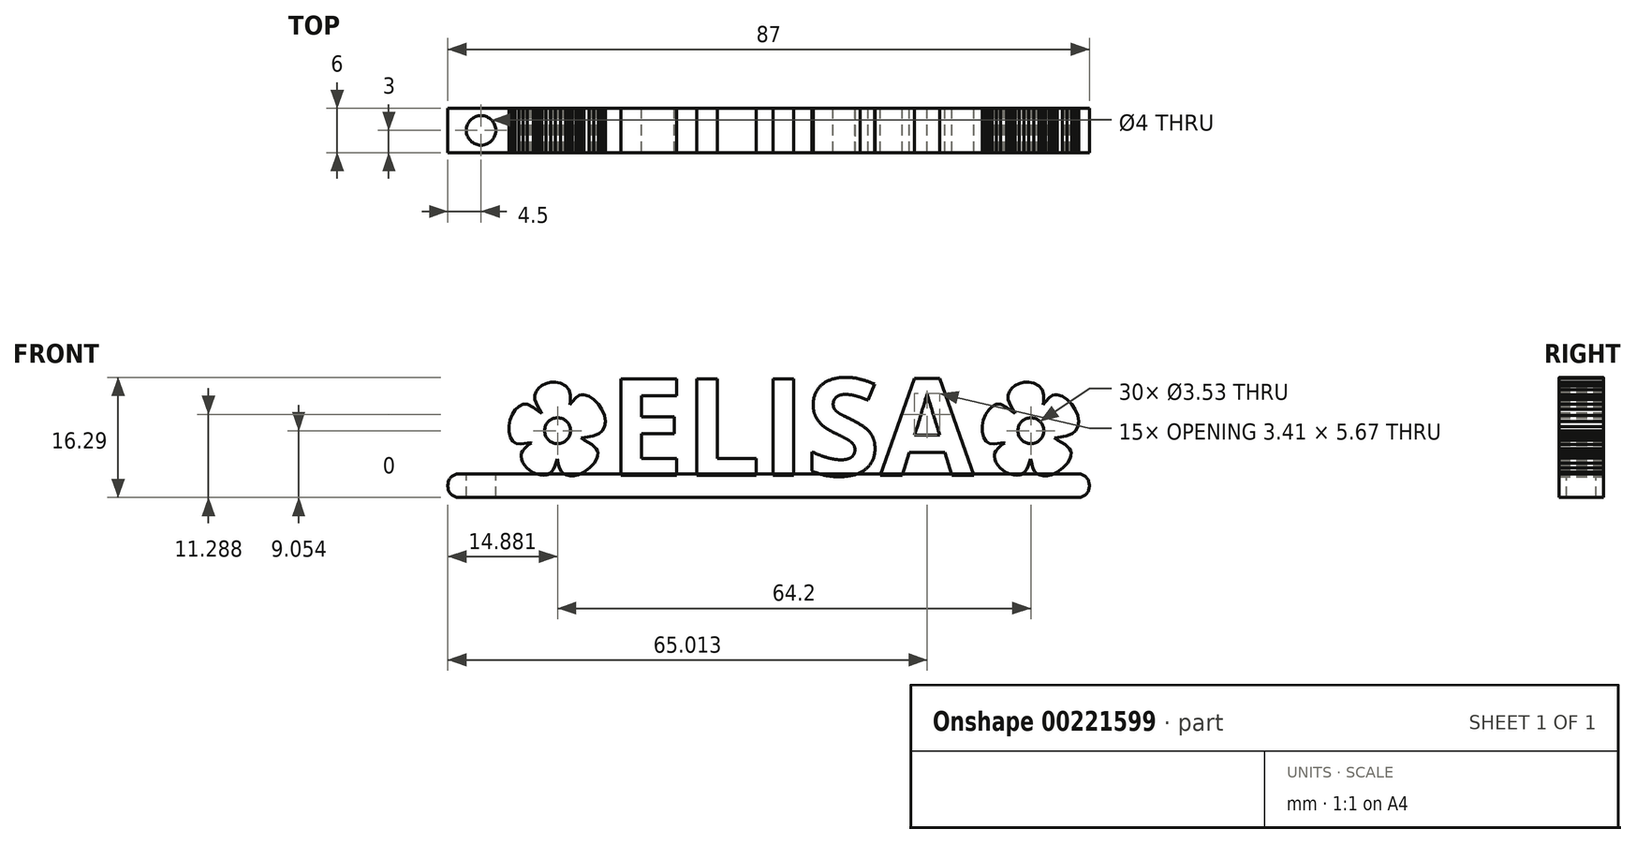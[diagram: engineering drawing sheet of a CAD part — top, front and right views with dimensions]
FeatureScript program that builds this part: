
annotation { "Feature Type Name" : "Feature", "Feature Type Description" : "" }
export const myFeature = defineFeature(function(context is Context, id is Id, definition is map)
    precondition{}
    {
        {
            var Q0;
            Q0=qCreatedBy(makeId("Front.planeOp"),FACE);
            var sketch = newSketch(context, id + "F0", { "sketchPlane" : qUnion([Q0])});
            skText(sketch, "E0", { "text": "   ELISA", "fontName": "OpenSans-Bold.ttf"});
            skLineSegment(sketch, "E1.0.0", {"start": v(-9.3, 0.1) * mm, "end": v(-8.53, 0.46) * mm});
            skLineSegment(sketch, "E1.0.1", {"start": v(-8.53, 0.46) * mm, "end": v(-7.79, 1.02) * mm});
            skLineSegment(sketch, "E1.0.2", {"start": v(-7.79, 1.02) * mm, "end": v(-7.18, 1.67) * mm});
            skLineSegment(sketch, "E1.0.3", {"start": v(-7.18, 1.67) * mm, "end": v(-6.78, 2.35) * mm});
            skLineSegment(sketch, "E1.0.4", {"start": v(-6.78, 2.35) * mm, "end": v(-6.68, 2.7) * mm});
            skLineSegment(sketch, "E1.0.5", {"start": v(-6.68, 2.7) * mm, "end": v(-6.67, 3.02) * mm});
            skLineSegment(sketch, "E1.0.6", {"start": v(-6.67, 3.02) * mm, "end": v(-6.73, 3.33) * mm});
            skLineSegment(sketch, "E1.0.7", {"start": v(-6.73, 3.33) * mm, "end": v(-6.89, 3.62) * mm});
            skLineSegment(sketch, "E1.0.8", {"start": v(-6.89, 3.62) * mm, "end": v(-7.48, 4.2) * mm});
            skLineSegment(sketch, "E1.0.9", {"start": v(-7.48, 4.2) * mm, "end": v(-8.5, 4.79) * mm});
            skLineSegment(sketch, "E1.0.10", {"start": v(-8.5, 4.79) * mm, "end": v(-8.93, 5.06) * mm});
            skLineSegment(sketch, "E1.0.11", {"start": v(-8.93, 5.06) * mm, "end": v(-8.42, 5.16) * mm});
            skLineSegment(sketch, "E1.0.12", {"start": v(-8.42, 5.16) * mm, "end": v(-7.31, 5.37) * mm});
            skLineSegment(sketch, "E1.0.13", {"start": v(-7.31, 5.37) * mm, "end": v(-6.55, 5.65) * mm});
            skLineSegment(sketch, "E1.0.14", {"start": v(-6.55, 5.65) * mm, "end": v(-6.05, 6.04) * mm});
            skLineSegment(sketch, "E1.0.15", {"start": v(-6.05, 6.04) * mm, "end": v(-5.76, 6.58) * mm});
            skLineSegment(sketch, "E1.0.16", {"start": v(-5.76, 6.58) * mm, "end": v(-5.64, 7.33) * mm});
            skLineSegment(sketch, "E1.0.17", {"start": v(-5.64, 7.33) * mm, "end": v(-5.78, 8.14) * mm});
            skLineSegment(sketch, "E1.0.18", {"start": v(-5.78, 8.14) * mm, "end": v(-6.1, 8.93) * mm});
            skLineSegment(sketch, "E1.0.19", {"start": v(-6.1, 8.93) * mm, "end": v(-6.6, 9.67) * mm});
            skLineSegment(sketch, "E1.0.20", {"start": v(-6.6, 9.67) * mm, "end": v(-7.2, 10.28) * mm});
            skLineSegment(sketch, "E1.0.21", {"start": v(-7.2, 10.28) * mm, "end": v(-7.86, 10.72) * mm});
            skLineSegment(sketch, "E1.0.22", {"start": v(-7.86, 10.72) * mm, "end": v(-8.55, 10.93) * mm});
            skLineSegment(sketch, "E1.0.23", {"start": v(-8.55, 10.93) * mm, "end": v(-8.88, 10.93) * mm});
            skLineSegment(sketch, "E1.0.24", {"start": v(-8.88, 10.93) * mm, "end": v(-9.2, 10.85) * mm});
            skLineSegment(sketch, "E1.0.25", {"start": v(-9.2, 10.85) * mm, "end": v(-9.65, 10.56) * mm});
            skLineSegment(sketch, "E1.0.26", {"start": v(-9.65, 10.56) * mm, "end": v(-10.14, 9.98) * mm});
            skLineSegment(sketch, "E1.0.27", {"start": v(-10.14, 9.98) * mm, "end": v(-10.45, 9.58) * mm});
            skLineSegment(sketch, "E1.0.28", {"start": v(-10.45, 9.58) * mm, "end": v(-10.4, 10.03) * mm});
            skLineSegment(sketch, "E1.0.29", {"start": v(-10.4, 10.03) * mm, "end": v(-10.4, 10.93) * mm});
            skLineSegment(sketch, "E1.0.30", {"start": v(-10.4, 10.93) * mm, "end": v(-10.6, 11.63) * mm});
            skLineSegment(sketch, "E1.0.31", {"start": v(-10.6, 11.63) * mm, "end": v(-11.04, 12.15) * mm});
            skLineSegment(sketch, "E1.0.32", {"start": v(-11.04, 12.15) * mm, "end": v(-11.71, 12.5) * mm});
            skLineSegment(sketch, "E1.0.33", {"start": v(-11.71, 12.5) * mm, "end": v(-12.4, 12.64) * mm});
            skLineSegment(sketch, "E1.0.34", {"start": v(-12.4, 12.64) * mm, "end": v(-13.07, 12.62) * mm});
            skLineSegment(sketch, "E1.0.35", {"start": v(-13.07, 12.62) * mm, "end": v(-13.7, 12.47) * mm});
            skLineSegment(sketch, "E1.0.36", {"start": v(-13.7, 12.47) * mm, "end": v(-14.26, 12.2) * mm});
            skLineSegment(sketch, "E1.0.37", {"start": v(-14.26, 12.2) * mm, "end": v(-14.72, 11.83) * mm});
            skLineSegment(sketch, "E1.0.38", {"start": v(-14.72, 11.83) * mm, "end": v(-15.05, 11.38) * mm});
            skLineSegment(sketch, "E1.0.39", {"start": v(-15.05, 11.38) * mm, "end": v(-15.22, 10.87) * mm});
            skLineSegment(sketch, "E1.0.40", {"start": v(-15.22, 10.87) * mm, "end": v(-15.2, 10.3) * mm});
            skLineSegment(sketch, "E1.0.41", {"start": v(-15.2, 10.3) * mm, "end": v(-14.83, 9.4) * mm});
            skLineSegment(sketch, "E1.0.42", {"start": v(-14.83, 9.4) * mm, "end": v(-14.35, 8.55) * mm});
            skLineSegment(sketch, "E1.0.43", {"start": v(-14.35, 8.55) * mm, "end": v(-14.3, 8.4) * mm});
            skLineSegment(sketch, "E1.0.44", {"start": v(-14.3, 8.4) * mm, "end": v(-14.48, 8.53) * mm});
            skLineSegment(sketch, "E1.0.45", {"start": v(-14.48, 8.53) * mm, "end": v(-15.4, 9.23) * mm});
            skLineSegment(sketch, "E1.0.46", {"start": v(-15.4, 9.23) * mm, "end": v(-16.22, 9.63) * mm});
            skLineSegment(sketch, "E1.0.47", {"start": v(-16.22, 9.63) * mm, "end": v(-16.8, 9.63) * mm});
            skLineSegment(sketch, "E1.0.48", {"start": v(-16.8, 9.63) * mm, "end": v(-17.36, 9.37) * mm});
            skLineSegment(sketch, "E1.0.49", {"start": v(-17.36, 9.37) * mm, "end": v(-17.85, 8.9) * mm});
            skLineSegment(sketch, "E1.0.50", {"start": v(-17.85, 8.9) * mm, "end": v(-18.26, 8.26) * mm});
            skLineSegment(sketch, "E1.0.51", {"start": v(-18.26, 8.26) * mm, "end": v(-18.56, 7.51) * mm});
            skLineSegment(sketch, "E1.0.52", {"start": v(-18.56, 7.51) * mm, "end": v(-18.72, 6.71) * mm});
            skLineSegment(sketch, "E1.0.53", {"start": v(-18.72, 6.71) * mm, "end": v(-18.72, 5.9) * mm});
            skLineSegment(sketch, "E1.0.54", {"start": v(-18.72, 5.9) * mm, "end": v(-18.52, 5.16) * mm});
            skLineSegment(sketch, "E1.0.55", {"start": v(-18.52, 5.16) * mm, "end": v(-18.2, 4.64) * mm});
            skLineSegment(sketch, "E1.0.56", {"start": v(-18.2, 4.64) * mm, "end": v(-17.75, 4.36) * mm});
            skLineSegment(sketch, "E1.0.57", {"start": v(-17.75, 4.36) * mm, "end": v(-17.1, 4.27) * mm});
            skLineSegment(sketch, "E1.0.58", {"start": v(-17.1, 4.27) * mm, "end": v(-16.21, 4.37) * mm});
            skLineSegment(sketch, "E1.0.59", {"start": v(-16.21, 4.37) * mm, "end": v(-15.7, 4.43) * mm});
            skLineSegment(sketch, "E1.0.60", {"start": v(-15.7, 4.43) * mm, "end": v(-15.67, 4.4) * mm});
            skLineSegment(sketch, "E1.0.61", {"start": v(-15.67, 4.4) * mm, "end": v(-15.78, 4.33) * mm});
            skLineSegment(sketch, "E1.0.62", {"start": v(-15.78, 4.33) * mm, "end": v(-16.17, 4.07) * mm});
            skLineSegment(sketch, "E1.0.63", {"start": v(-16.17, 4.07) * mm, "end": v(-16.55, 3.71) * mm});
            skLineSegment(sketch, "E1.0.64", {"start": v(-16.55, 3.71) * mm, "end": v(-16.87, 3.33) * mm});
            skLineSegment(sketch, "E1.0.65", {"start": v(-16.87, 3.33) * mm, "end": v(-17.04, 3) * mm});
            skLineSegment(sketch, "E1.0.66", {"start": v(-17.04, 3) * mm, "end": v(-17.08, 2.6) * mm});
            skLineSegment(sketch, "E1.0.67", {"start": v(-17.08, 2.6) * mm, "end": v(-17.02, 2.2) * mm});
            skLineSegment(sketch, "E1.0.68", {"start": v(-17.02, 2.2) * mm, "end": v(-16.87, 1.78) * mm});
            skLineSegment(sketch, "E1.0.69", {"start": v(-16.87, 1.78) * mm, "end": v(-16.62, 1.39) * mm});
            skLineSegment(sketch, "E1.0.70", {"start": v(-16.62, 1.39) * mm, "end": v(-16.3, 1.02) * mm});
            skLineSegment(sketch, "E1.0.71", {"start": v(-16.3, 1.02) * mm, "end": v(-15.9, 0.69) * mm});
            skLineSegment(sketch, "E1.0.72", {"start": v(-15.9, 0.69) * mm, "end": v(-15.45, 0.4) * mm});
            skLineSegment(sketch, "E1.0.73", {"start": v(-15.45, 0.4) * mm, "end": v(-14.95, 0.2) * mm});
            skLineSegment(sketch, "E1.0.74", {"start": v(-14.95, 0.2) * mm, "end": v(-14.44, 0.06) * mm});
            skLineSegment(sketch, "E1.0.75", {"start": v(-14.44, 0.06) * mm, "end": v(-13.98, 0.02) * mm});
            skLineSegment(sketch, "E1.0.76", {"start": v(-13.98, 0.02) * mm, "end": v(-13.58, 0.08) * mm});
            skLineSegment(sketch, "E1.0.77", {"start": v(-13.58, 0.08) * mm, "end": v(-13.23, 0.23) * mm});
            skLineSegment(sketch, "E1.0.78", {"start": v(-13.23, 0.23) * mm, "end": v(-12.92, 0.49) * mm});
            skLineSegment(sketch, "E1.0.79", {"start": v(-12.92, 0.49) * mm, "end": v(-12.67, 0.84) * mm});
            skLineSegment(sketch, "E1.0.80", {"start": v(-12.67, 0.84) * mm, "end": v(-12.46, 1.28) * mm});
            skLineSegment(sketch, "E1.0.81", {"start": v(-12.46, 1.28) * mm, "end": v(-12.3, 1.83) * mm});
            skLineSegment(sketch, "E1.0.82", {"start": v(-12.3, 1.83) * mm, "end": v(-12.19, 2.26) * mm});
            skLineSegment(sketch, "E1.0.83", {"start": v(-12.19, 2.26) * mm, "end": v(-12.13, 2.1) * mm});
            skLineSegment(sketch, "E1.0.84", {"start": v(-12.13, 2.1) * mm, "end": v(-12.01, 1.53) * mm});
            skLineSegment(sketch, "E1.0.85", {"start": v(-12.01, 1.53) * mm, "end": v(-11.82, 1) * mm});
            skLineSegment(sketch, "E1.0.86", {"start": v(-11.82, 1) * mm, "end": v(-11.6, 0.55) * mm});
            skLineSegment(sketch, "E1.0.87", {"start": v(-11.6, 0.55) * mm, "end": v(-11.35, 0.26) * mm});
            skLineSegment(sketch, "E1.0.88", {"start": v(-11.35, 0.26) * mm, "end": v(-10.95, 0.05) * mm});
            skLineSegment(sketch, "E1.0.89", {"start": v(-10.95, 0.05) * mm, "end": v(-10.46, -0.04) * mm});
            skLineSegment(sketch, "E1.0.90", {"start": v(-10.46, -0.04) * mm, "end": v(-9.9, -0.03) * mm});
            skLineSegment(sketch, "E1.0.91", {"start": v(-9.9, -0.03) * mm, "end": v(-9.3, 0.1) * mm});
            skCircle(sketch, "E2", {"center": v(-12.12, 6.05) * mm, "radius": 1.77 * mm});
            skCircle(sketch, "E3.1.0.0", {"center": v(52.08, 6.05) * mm, "radius": 1.77 * mm});
            skLineSegment(sketch, "E3.1.0.1", {"start": v(53.75, 9.58) * mm, "end": v(53.8, 10.03) * mm});
            skLineSegment(sketch, "E3.1.0.2", {"start": v(57, 10.28) * mm, "end": v(56.34, 10.72) * mm});
            skLineSegment(sketch, "E3.1.0.3", {"start": v(45.48, 5.9) * mm, "end": v(45.68, 5.16) * mm});
            skLineSegment(sketch, "E3.1.0.4", {"start": v(49.94, 12.2) * mm, "end": v(49.48, 11.83) * mm});
            skLineSegment(sketch, "E3.1.0.5", {"start": v(47.9, 1.02) * mm, "end": v(48.3, 0.69) * mm});
            skLineSegment(sketch, "E3.1.0.6", {"start": v(47.98, 9.63) * mm, "end": v(47.4, 9.63) * mm});
            skLineSegment(sketch, "E3.1.0.7", {"start": v(45.64, 7.51) * mm, "end": v(45.48, 6.71) * mm});
            skLineSegment(sketch, "E3.1.0.8", {"start": v(48.8, 9.23) * mm, "end": v(47.98, 9.63) * mm});
            skLineSegment(sketch, "E3.1.0.9", {"start": v(47.4, 9.63) * mm, "end": v(46.84, 9.37) * mm});
            skLineSegment(sketch, "E3.1.0.10", {"start": v(54.06, 9.98) * mm, "end": v(53.75, 9.58) * mm});
            skLineSegment(sketch, "E3.1.0.11", {"start": v(53.6, 11.63) * mm, "end": v(53.16, 12.15) * mm});
            skLineSegment(sketch, "E3.1.0.12", {"start": v(53.16, 12.15) * mm, "end": v(52.49, 12.5) * mm});
            skLineSegment(sketch, "E3.1.0.13", {"start": v(53.8, 10.93) * mm, "end": v(53.6, 11.63) * mm});
            skLineSegment(sketch, "E3.1.0.14", {"start": v(48.75, 0.4) * mm, "end": v(49.25, 0.2) * mm});
            skLineSegment(sketch, "E3.1.0.15", {"start": v(54.3, -0.03) * mm, "end": v(54.9, 0.1) * mm});
            skLineSegment(sketch, "E3.1.0.16", {"start": v(45.48, 6.71) * mm, "end": v(45.48, 5.9) * mm});
            skLineSegment(sketch, "E3.1.0.17", {"start": v(54.9, 0.1) * mm, "end": v(55.67, 0.46) * mm});
            skLineSegment(sketch, "E3.1.0.18", {"start": v(48.3, 0.69) * mm, "end": v(48.75, 0.4) * mm});
            skLineSegment(sketch, "E3.1.0.19", {"start": v(45.68, 5.16) * mm, "end": v(46, 4.64) * mm});
            skLineSegment(sketch, "E3.1.0.20", {"start": v(56.89, 5.37) * mm, "end": v(57.65, 5.65) * mm});
            skLineSegment(sketch, "E3.1.0.21", {"start": v(55.67, 0.46) * mm, "end": v(56.41, 1.02) * mm});
            skLineSegment(sketch, "E3.1.0.22", {"start": v(57.6, 9.67) * mm, "end": v(57, 10.28) * mm});
            skLineSegment(sketch, "E3.1.0.23", {"start": v(53.8, 10.03) * mm, "end": v(53.8, 10.93) * mm});
            skLineSegment(sketch, "E3.1.0.24", {"start": v(46.84, 9.37) * mm, "end": v(46.35, 8.9) * mm});
            skLineSegment(sketch, "E3.1.0.25", {"start": v(52.49, 12.5) * mm, "end": v(51.8, 12.64) * mm});
            skLineSegment(sketch, "E3.1.0.26", {"start": v(51.13, 12.62) * mm, "end": v(50.5, 12.47) * mm});
            skLineSegment(sketch, "E3.1.0.27", {"start": v(57.02, 1.67) * mm, "end": v(57.42, 2.35) * mm});
            skLineSegment(sketch, "E3.1.0.28", {"start": v(58.1, 8.93) * mm, "end": v(57.6, 9.67) * mm});
            skLineSegment(sketch, "E3.1.0.29", {"start": v(51.8, 12.64) * mm, "end": v(51.13, 12.62) * mm});
            skLineSegment(sketch, "E3.1.0.30", {"start": v(56.41, 1.02) * mm, "end": v(57.02, 1.67) * mm});
            skLineSegment(sketch, "E3.1.0.31", {"start": v(46.35, 8.9) * mm, "end": v(45.94, 8.26) * mm});
            skLineSegment(sketch, "E3.1.0.32", {"start": v(45.94, 8.26) * mm, "end": v(45.64, 7.51) * mm});
            skLineSegment(sketch, "E3.1.0.33", {"start": v(50.5, 12.47) * mm, "end": v(49.94, 12.2) * mm});
            skLineSegment(sketch, "E3.1.0.34", {"start": v(57.42, 2.35) * mm, "end": v(57.52, 2.7) * mm});
            skLineSegment(sketch, "E3.1.0.35", {"start": v(47.4, 9.63) * mm, "end": v(46.84, 9.37) * mm});
            skLineSegment(sketch, "E3.1.0.36", {"start": v(51.8, 12.64) * mm, "end": v(51.13, 12.62) * mm});
            skLineSegment(sketch, "E3.1.0.37", {"start": v(56.89, 5.37) * mm, "end": v(57.65, 5.65) * mm});
            skLineSegment(sketch, "E3.1.0.38", {"start": v(53.25, 0.05) * mm, "end": v(53.74, -0.04) * mm});
            skLineSegment(sketch, "E3.1.0.39", {"start": v(58.1, 8.93) * mm, "end": v(57.6, 9.67) * mm});
            skLineSegment(sketch, "E3.1.0.40", {"start": v(54.3, -0.03) * mm, "end": v(54.9, 0.1) * mm});
            skLineSegment(sketch, "E3.1.0.41", {"start": v(54.06, 9.98) * mm, "end": v(53.75, 9.58) * mm});
            skLineSegment(sketch, "E3.1.0.42", {"start": v(56.41, 1.02) * mm, "end": v(57.02, 1.67) * mm});
            skLineSegment(sketch, "E3.1.0.43", {"start": v(57.42, 2.35) * mm, "end": v(57.52, 2.7) * mm});
            skLineSegment(sketch, "E3.1.0.44", {"start": v(45.48, 6.71) * mm, "end": v(45.48, 5.9) * mm});
            skLineSegment(sketch, "E3.1.0.45", {"start": v(54.9, 0.1) * mm, "end": v(55.67, 0.46) * mm});
            skLineSegment(sketch, "E3.1.0.46", {"start": v(51.13, 12.62) * mm, "end": v(50.5, 12.47) * mm});
            skLineSegment(sketch, "E3.1.0.47", {"start": v(49.94, 12.2) * mm, "end": v(49.48, 11.83) * mm});
            skLineSegment(sketch, "E3.1.0.48", {"start": v(48.75, 0.4) * mm, "end": v(49.25, 0.2) * mm});
            skLineSegment(sketch, "E3.1.0.49", {"start": v(53.8, 10.03) * mm, "end": v(53.8, 10.93) * mm});
            skLineSegment(sketch, "E3.1.0.50", {"start": v(53.75, 9.58) * mm, "end": v(53.8, 10.03) * mm});
            skLineSegment(sketch, "E3.1.0.51", {"start": v(53.74, -0.04) * mm, "end": v(54.3, -0.03) * mm});
            skLineSegment(sketch, "E3.1.0.52", {"start": v(47.98, 9.63) * mm, "end": v(47.4, 9.63) * mm});
            skLineSegment(sketch, "E3.1.0.53", {"start": v(53.8, 10.93) * mm, "end": v(53.6, 11.63) * mm});
            skLineSegment(sketch, "E3.1.0.54", {"start": v(57, 10.28) * mm, "end": v(56.34, 10.72) * mm});
            skLineSegment(sketch, "E3.1.0.55", {"start": v(46.35, 8.9) * mm, "end": v(45.94, 8.26) * mm});
            skLineSegment(sketch, "E3.1.0.56", {"start": v(48.3, 0.69) * mm, "end": v(48.75, 0.4) * mm});
            skLineSegment(sketch, "E3.1.0.57", {"start": v(52.49, 12.5) * mm, "end": v(51.8, 12.64) * mm});
            skLineSegment(sketch, "E3.1.0.58", {"start": v(46.84, 9.37) * mm, "end": v(46.35, 8.9) * mm});
            skLineSegment(sketch, "E3.1.0.59", {"start": v(45.48, 5.9) * mm, "end": v(45.68, 5.16) * mm});
            skLineSegment(sketch, "E3.1.0.60", {"start": v(53.16, 12.15) * mm, "end": v(52.49, 12.5) * mm});
            skLineSegment(sketch, "E3.1.0.61", {"start": v(48.8, 9.23) * mm, "end": v(47.98, 9.63) * mm});
            skLineSegment(sketch, "E3.1.0.62", {"start": v(55.67, 0.46) * mm, "end": v(56.41, 1.02) * mm});
            skLineSegment(sketch, "E3.1.0.63", {"start": v(53.6, 11.63) * mm, "end": v(53.16, 12.15) * mm});
            skLineSegment(sketch, "E3.1.0.64", {"start": v(45.94, 8.26) * mm, "end": v(45.64, 7.51) * mm});
            skLineSegment(sketch, "E3.1.0.65", {"start": v(57.02, 1.67) * mm, "end": v(57.42, 2.35) * mm});
            skLineSegment(sketch, "E3.1.0.66", {"start": v(45.64, 7.51) * mm, "end": v(45.48, 6.71) * mm});
            skLineSegment(sketch, "E3.1.0.67", {"start": v(47.9, 1.02) * mm, "end": v(48.3, 0.69) * mm});
            skLineSegment(sketch, "E3.1.0.68", {"start": v(45.68, 5.16) * mm, "end": v(46, 4.64) * mm});
            skLineSegment(sketch, "E3.1.0.69", {"start": v(50.5, 12.47) * mm, "end": v(49.94, 12.2) * mm});
            skLineSegment(sketch, "E3.1.0.70", {"start": v(57.6, 9.67) * mm, "end": v(57, 10.28) * mm});
            skLineSegment(sketch, "E3.1.0.71", {"start": v(49.48, 11.83) * mm, "end": v(49.15, 11.38) * mm});
            skLineSegment(sketch, "E3.1.0.72", {"start": v(56.34, 10.72) * mm, "end": v(55.65, 10.93) * mm});
            skLineSegment(sketch, "E3.1.0.73", {"start": v(58.15, 6.04) * mm, "end": v(58.44, 6.58) * mm});
            skLineSegment(sketch, "E3.1.0.74", {"start": v(57.52, 2.7) * mm, "end": v(57.53, 3.02) * mm});
            skLineSegment(sketch, "E3.1.0.75", {"start": v(55.65, 10.93) * mm, "end": v(55.32, 10.93) * mm});
            skLineSegment(sketch, "E3.1.0.76", {"start": v(46, 4.64) * mm, "end": v(46.45, 4.36) * mm});
            skLineSegment(sketch, "E3.1.0.77", {"start": v(55, 10.85) * mm, "end": v(54.55, 10.56) * mm});
            skLineSegment(sketch, "E3.1.0.78", {"start": v(55.78, 5.16) * mm, "end": v(56.89, 5.37) * mm});
            skLineSegment(sketch, "E3.1.0.79", {"start": v(57.53, 3.02) * mm, "end": v(57.47, 3.33) * mm});
            skLineSegment(sketch, "E3.1.0.80", {"start": v(57.47, 3.33) * mm, "end": v(57.31, 3.62) * mm});
            skLineSegment(sketch, "E3.1.0.81", {"start": v(56.72, 4.2) * mm, "end": v(55.7, 4.79) * mm});
            skLineSegment(sketch, "E3.1.0.82", {"start": v(58.56, 7.33) * mm, "end": v(58.42, 8.14) * mm});
            skLineSegment(sketch, "E3.1.0.83", {"start": v(47.58, 1.39) * mm, "end": v(47.9, 1.02) * mm});
            skLineSegment(sketch, "E3.1.0.84", {"start": v(49.76, 0.06) * mm, "end": v(50.22, 0.02) * mm});
            skLineSegment(sketch, "E3.1.0.85", {"start": v(55.27, 5.06) * mm, "end": v(55.78, 5.16) * mm});
            skLineSegment(sketch, "E3.1.0.86", {"start": v(52.85, 0.26) * mm, "end": v(53.25, 0.05) * mm});
            skLineSegment(sketch, "E3.1.0.87", {"start": v(49.15, 11.38) * mm, "end": v(48.98, 10.87) * mm});
            skLineSegment(sketch, "E3.1.0.88", {"start": v(58.44, 6.58) * mm, "end": v(58.56, 7.33) * mm});
            skLineSegment(sketch, "E3.1.0.89", {"start": v(53.25, 0.05) * mm, "end": v(53.74, -0.04) * mm});
            skLineSegment(sketch, "E3.1.0.90", {"start": v(55.7, 4.79) * mm, "end": v(55.27, 5.06) * mm});
            skLineSegment(sketch, "E3.1.0.91", {"start": v(49.25, 0.2) * mm, "end": v(49.76, 0.06) * mm});
            skLineSegment(sketch, "E3.1.0.92", {"start": v(49, 10.3) * mm, "end": v(49.37, 9.4) * mm});
            skLineSegment(sketch, "E3.1.0.93", {"start": v(47.33, 1.78) * mm, "end": v(47.58, 1.39) * mm});
            skLineSegment(sketch, "E3.1.0.94", {"start": v(57.31, 3.62) * mm, "end": v(56.72, 4.2) * mm});
            skLineSegment(sketch, "E3.1.0.95", {"start": v(53.74, -0.04) * mm, "end": v(54.3, -0.03) * mm});
            skLineSegment(sketch, "E3.1.0.96", {"start": v(48.98, 10.87) * mm, "end": v(49, 10.3) * mm});
            skLineSegment(sketch, "E3.1.0.97", {"start": v(57.65, 5.65) * mm, "end": v(58.15, 6.04) * mm});
            skLineSegment(sketch, "E3.1.0.98", {"start": v(55.32, 10.93) * mm, "end": v(55, 10.85) * mm});
            skLineSegment(sketch, "E3.1.0.99", {"start": v(54.55, 10.56) * mm, "end": v(54.06, 9.98) * mm});
            skLineSegment(sketch, "E3.1.0.100", {"start": v(50.22, 0.02) * mm, "end": v(50.62, 0.08) * mm});
            skLineSegment(sketch, "E3.1.0.101", {"start": v(47.18, 2.2) * mm, "end": v(47.33, 1.78) * mm});
            skLineSegment(sketch, "E3.1.0.102", {"start": v(58.42, 8.14) * mm, "end": v(58.1, 8.93) * mm});
            skLineSegment(sketch, "E3.1.0.103", {"start": v(55.7, 4.79) * mm, "end": v(55.27, 5.06) * mm});
            skLineSegment(sketch, "E3.1.0.104", {"start": v(55.27, 5.06) * mm, "end": v(55.78, 5.16) * mm});
            skLineSegment(sketch, "E3.1.0.105", {"start": v(46, 4.64) * mm, "end": v(46.45, 4.36) * mm});
            skLineSegment(sketch, "E3.1.0.106", {"start": v(52.6, 0.55) * mm, "end": v(52.85, 0.26) * mm});
            skLineSegment(sketch, "E3.1.0.107", {"start": v(52.85, 0.26) * mm, "end": v(53.25, 0.05) * mm});
            skLineSegment(sketch, "E3.1.0.108", {"start": v(47.33, 1.78) * mm, "end": v(47.58, 1.39) * mm});
            skLineSegment(sketch, "E3.1.0.109", {"start": v(57.31, 3.62) * mm, "end": v(56.72, 4.2) * mm});
            skLineSegment(sketch, "E3.1.0.110", {"start": v(55.78, 5.16) * mm, "end": v(56.89, 5.37) * mm});
            skLineSegment(sketch, "E3.1.0.111", {"start": v(49, 10.3) * mm, "end": v(49.37, 9.4) * mm});
            skLineSegment(sketch, "E3.1.0.112", {"start": v(57.65, 5.65) * mm, "end": v(58.15, 6.04) * mm});
            skLineSegment(sketch, "E3.1.0.113", {"start": v(54.55, 10.56) * mm, "end": v(54.06, 9.98) * mm});
            skLineSegment(sketch, "E3.1.0.114", {"start": v(58.44, 6.58) * mm, "end": v(58.56, 7.33) * mm});
            skLineSegment(sketch, "E3.1.0.115", {"start": v(48.98, 10.87) * mm, "end": v(49, 10.3) * mm});
            skLineSegment(sketch, "E3.1.0.116", {"start": v(55.32, 10.93) * mm, "end": v(55, 10.85) * mm});
            skLineSegment(sketch, "E3.1.0.117", {"start": v(50.22, 0.02) * mm, "end": v(50.62, 0.08) * mm});
            skLineSegment(sketch, "E3.1.0.118", {"start": v(55, 10.85) * mm, "end": v(54.55, 10.56) * mm});
            skLineSegment(sketch, "E3.1.0.119", {"start": v(49.76, 0.06) * mm, "end": v(50.22, 0.02) * mm});
            skLineSegment(sketch, "E3.1.0.120", {"start": v(49.25, 0.2) * mm, "end": v(49.76, 0.06) * mm});
            skLineSegment(sketch, "E3.1.0.121", {"start": v(56.72, 4.2) * mm, "end": v(55.7, 4.79) * mm});
            skLineSegment(sketch, "E3.1.0.122", {"start": v(58.15, 6.04) * mm, "end": v(58.44, 6.58) * mm});
            skLineSegment(sketch, "E3.1.0.123", {"start": v(47.12, 2.6) * mm, "end": v(47.18, 2.2) * mm});
            skLineSegment(sketch, "E3.1.0.124", {"start": v(57.52, 2.7) * mm, "end": v(57.53, 3.02) * mm});
            skLineSegment(sketch, "E3.1.0.125", {"start": v(47.58, 1.39) * mm, "end": v(47.9, 1.02) * mm});
            skLineSegment(sketch, "E3.1.0.126", {"start": v(58.42, 8.14) * mm, "end": v(58.1, 8.93) * mm});
            skLineSegment(sketch, "E3.1.0.127", {"start": v(58.56, 7.33) * mm, "end": v(58.42, 8.14) * mm});
            skLineSegment(sketch, "E3.1.0.128", {"start": v(57.53, 3.02) * mm, "end": v(57.47, 3.33) * mm});
            skLineSegment(sketch, "E3.1.0.129", {"start": v(47.18, 2.2) * mm, "end": v(47.33, 1.78) * mm});
            skLineSegment(sketch, "E3.1.0.130", {"start": v(57.47, 3.33) * mm, "end": v(57.31, 3.62) * mm});
            skLineSegment(sketch, "E3.1.0.131", {"start": v(49.15, 11.38) * mm, "end": v(48.98, 10.87) * mm});
            skLineSegment(sketch, "E3.1.0.132", {"start": v(55.65, 10.93) * mm, "end": v(55.32, 10.93) * mm});
            skLineSegment(sketch, "E3.1.0.133", {"start": v(56.34, 10.72) * mm, "end": v(55.65, 10.93) * mm});
            skLineSegment(sketch, "E3.1.0.134", {"start": v(49.48, 11.83) * mm, "end": v(49.15, 11.38) * mm});
            skLineSegment(sketch, "E3.1.0.135", {"start": v(47.12, 2.6) * mm, "end": v(47.18, 2.2) * mm});
            skLineSegment(sketch, "E3.1.0.136", {"start": v(47.99, 4.37) * mm, "end": v(48.5, 4.43) * mm});
            skLineSegment(sketch, "E3.1.0.137", {"start": v(52.19, 1.53) * mm, "end": v(52.38, 1) * mm});
            skLineSegment(sketch, "E3.1.0.138", {"start": v(48.42, 4.33) * mm, "end": v(48.03, 4.07) * mm});
            skLineSegment(sketch, "E3.1.0.139", {"start": v(50.97, 0.23) * mm, "end": v(51.28, 0.49) * mm});
            skLineSegment(sketch, "E3.1.0.140", {"start": v(51.53, 0.84) * mm, "end": v(51.74, 1.28) * mm});
            skLineSegment(sketch, "E3.1.0.141", {"start": v(52.38, 1) * mm, "end": v(52.6, 0.55) * mm});
            skLineSegment(sketch, "E3.1.0.142", {"start": v(48.03, 4.07) * mm, "end": v(47.65, 3.71) * mm});
            skLineSegment(sketch, "E3.1.0.143", {"start": v(52.07, 2.1) * mm, "end": v(52.19, 1.53) * mm});
            skLineSegment(sketch, "E3.1.0.144", {"start": v(51.28, 0.49) * mm, "end": v(51.53, 0.84) * mm});
            skLineSegment(sketch, "E3.1.0.145", {"start": v(47.1, 4.27) * mm, "end": v(47.99, 4.37) * mm});
            skLineSegment(sketch, "E3.1.0.146", {"start": v(47.65, 3.71) * mm, "end": v(47.33, 3.33) * mm});
            skLineSegment(sketch, "E3.1.0.147", {"start": v(46.45, 4.36) * mm, "end": v(47.1, 4.27) * mm});
            skLineSegment(sketch, "E3.1.0.148", {"start": v(51.74, 1.28) * mm, "end": v(51.9, 1.83) * mm});
            skLineSegment(sketch, "E3.1.0.149", {"start": v(52.01, 2.26) * mm, "end": v(52.07, 2.1) * mm});
            skLineSegment(sketch, "E3.1.0.150", {"start": v(47.33, 3.33) * mm, "end": v(47.16, 3) * mm});
            skLineSegment(sketch, "E3.1.0.151", {"start": v(52.6, 0.55) * mm, "end": v(52.85, 0.26) * mm});
            skLineSegment(sketch, "E3.1.0.152", {"start": v(51.9, 1.83) * mm, "end": v(52.01, 2.26) * mm});
            skLineSegment(sketch, "E3.1.0.153", {"start": v(47.16, 3) * mm, "end": v(47.12, 2.6) * mm});
            skLineSegment(sketch, "E3.1.0.154", {"start": v(50.62, 0.08) * mm, "end": v(50.97, 0.23) * mm});
            skLineSegment(sketch, "E3.1.0.155", {"start": v(48.53, 4.4) * mm, "end": v(48.42, 4.33) * mm});
            skLineSegment(sketch, "E3.1.0.156", {"start": v(52.01, 2.26) * mm, "end": v(52.07, 2.1) * mm});
            skLineSegment(sketch, "E3.1.0.157", {"start": v(47.1, 4.27) * mm, "end": v(47.99, 4.37) * mm});
            skLineSegment(sketch, "E3.1.0.158", {"start": v(52.19, 1.53) * mm, "end": v(52.38, 1) * mm});
            skLineSegment(sketch, "E3.1.0.159", {"start": v(48.5, 4.43) * mm, "end": v(48.53, 4.4) * mm});
            skLineSegment(sketch, "E3.1.0.160", {"start": v(47.65, 3.71) * mm, "end": v(47.33, 3.33) * mm});
            skLineSegment(sketch, "E3.1.0.161", {"start": v(46.45, 4.36) * mm, "end": v(47.1, 4.27) * mm});
            skLineSegment(sketch, "E3.1.0.162", {"start": v(47.99, 4.37) * mm, "end": v(48.5, 4.43) * mm});
            skLineSegment(sketch, "E3.1.0.163", {"start": v(50.62, 0.08) * mm, "end": v(50.97, 0.23) * mm});
            skLineSegment(sketch, "E3.1.0.164", {"start": v(48.03, 4.07) * mm, "end": v(47.65, 3.71) * mm});
            skLineSegment(sketch, "E3.1.0.165", {"start": v(52.07, 2.1) * mm, "end": v(52.19, 1.53) * mm});
            skLineSegment(sketch, "E3.1.0.166", {"start": v(51.9, 1.83) * mm, "end": v(52.01, 2.26) * mm});
            skLineSegment(sketch, "E3.1.0.167", {"start": v(48.42, 4.33) * mm, "end": v(48.03, 4.07) * mm});
            skLineSegment(sketch, "E3.1.0.168", {"start": v(50.97, 0.23) * mm, "end": v(51.28, 0.49) * mm});
            skLineSegment(sketch, "E3.1.0.169", {"start": v(47.16, 3) * mm, "end": v(47.12, 2.6) * mm});
            skLineSegment(sketch, "E3.1.0.170", {"start": v(52.38, 1) * mm, "end": v(52.6, 0.55) * mm});
            skLineSegment(sketch, "E3.1.0.171", {"start": v(51.28, 0.49) * mm, "end": v(51.53, 0.84) * mm});
            skLineSegment(sketch, "E3.1.0.172", {"start": v(51.53, 0.84) * mm, "end": v(51.74, 1.28) * mm});
            skLineSegment(sketch, "E3.1.0.173", {"start": v(47.33, 3.33) * mm, "end": v(47.16, 3) * mm});
            skLineSegment(sketch, "E3.1.0.174", {"start": v(51.74, 1.28) * mm, "end": v(51.9, 1.83) * mm});
            skLineSegment(sketch, "E3.1.0.175", {"start": v(48.53, 4.4) * mm, "end": v(48.42, 4.33) * mm});
            skLineSegment(sketch, "E3.1.0.176", {"start": v(48.5, 4.43) * mm, "end": v(48.53, 4.4) * mm});
            skLineSegment(sketch, "E3.1.0.177", {"start": v(49.9, 8.4) * mm, "end": v(49.72, 8.53) * mm});
            skLineSegment(sketch, "E3.1.0.178", {"start": v(49.85, 8.55) * mm, "end": v(49.9, 8.4) * mm});
            skLineSegment(sketch, "E3.1.0.179", {"start": v(49.37, 9.4) * mm, "end": v(49.85, 8.55) * mm});
            skLineSegment(sketch, "E3.1.0.180", {"start": v(49.72, 8.53) * mm, "end": v(48.8, 9.23) * mm});
            skLineSegment(sketch, "E3.1.0.181", {"start": v(49.85, 8.55) * mm, "end": v(49.9, 8.4) * mm});
            skLineSegment(sketch, "E3.1.0.182", {"start": v(49.37, 9.4) * mm, "end": v(49.85, 8.55) * mm});
            skLineSegment(sketch, "E3.1.0.183", {"start": v(49.72, 8.53) * mm, "end": v(48.8, 9.23) * mm});
            skLineSegment(sketch, "E3.1.0.184", {"start": v(49.9, 8.4) * mm, "end": v(49.72, 8.53) * mm});
            skLineSegment(sketch, "E3.direction1", {"start": v(-16.3, 1.02) * mm, "end": v(42.4, 1.02) * mm, "construction": true});
            const initialGuessF0  = {"E0": [-0.0195, 0, 1, 0, 0.01322]};
            skSetInitialGuess(sketch, initialGuessF0);
            skSolve(sketch);
        }
        {
            var Q0;
            Q0=qSketchRegion(id+"F0",true);
            extrude(context, id + "F1", {"entities" : qUnion([Q0]), "endBound" : BoundingType.SYMMETRIC, "depth" : 6 * mm});
        }
        {
            var Q0;
            Q0=qCreatedBy(makeId("Top.planeOp"),FACE);
            var sketch = newSketch(context, id + "F2", { "sketchPlane" : qUnion([Q0])});
            skLineSegment(sketch, "E4.bottom", {"start": v(-19.5, 3) * mm, "end": v(60, 3) * mm});
            skLineSegment(sketch, "E4.top", {"start": v(-19.5, -3) * mm, "end": v(60, -3) * mm});
            skLineSegment(sketch, "E4.left", {"start": v(-19.5, 3) * mm, "end": v(-19.5, -3) * mm});
            skLineSegment(sketch, "E4.right", {"start": v(60, 3) * mm, "end": v(60, -3) * mm});
            skSolve(sketch);
        }
        {
            var Q0;
            Q0=makeQuery(id+"F2.imprint","IMPRINT",FACE,{"disambiguationData":[TD([[makeQuery(id+"F2.imprint","IMPRINT",EDGE,{"derivedFrom":sQuery(id+"F2.wireOp",EDGE,"E4.bottom")}),-1.0]])]});
            extrude(context, id + "F3", {"entities" : qUnion([Q0]), "depth" : 0.2 * mm});
        }
        {
            var Q0;
            Q0=makeQuery(id+"F3.opExtrude","CAP_FACE",FACE,{"disambiguationData":[OSD([sQuery(id+"F2.wireOp",EDGE,"E4.bottom"),sQuery(id+"F2.wireOp",EDGE,"E4.top"),sQuery(id+"F2.wireOp",EDGE,"E4.left"),sQuery(id+"F2.wireOp",EDGE,"E4.right")])],"isStart":true});
            extrude(context, id + "F4", {"entities" : qUnion([Q0]), "depth" : 3 * mm});
        }
        {
            var Q0;
            {var subQ0=sQuery(id+"F2.wireOp",EDGE,"E4.left");Q0=makeQuery(id+"FaVoHrOpcFZXiYX_6.opBoolean","MERGE",FACE,{"derivedFrom":[makeQuery(id+"F3.opExtrude","SWEPT_FACE",FACE,{"disambiguationData":[OSD([subQ0])]}),makeQuery(id+"F4.opExtrude","SWEPT_FACE",FACE,{"disambiguationData":[OSD([subQ0])]})]});}
            var sketch = newSketch(context, id + "F5", { "sketchPlane" : qUnion([Q0])});
            skLineSegment(sketch, "E5.bottom", {"start": v(-3, -3) * mm, "end": v(3, -3) * mm});
            skLineSegment(sketch, "E5.top", {"start": v(-3, 0.2) * mm, "end": v(3, 0.2) * mm});
            skLineSegment(sketch, "E5.left", {"start": v(-3, -3) * mm, "end": v(-3, 0.2) * mm});
            skLineSegment(sketch, "E5.right", {"start": v(3, -3) * mm, "end": v(3, 0.2) * mm});
            skSolve(sketch);
        }
        {
            var Q0;
            Q0=qSketchRegion(id+"F5",true);
            extrude(context, id + "F6", {"entities" : qUnion([Q0]), "operationType" : NewBodyOperationType.ADD, "depth" : 7.5 * mm});
        }
        {
            var Q0;
            Q0=makeQuery(id+"F6.opExtrude","CAP_EDGE",EDGE,{"disambiguationData":[OSD([sQuery(id+"F5.wireOp",EDGE,"E5.bottom")])],"isStart":false});
            var Q1;
            Q1=makeQuery(id+"F6.opExtrude","CAP_EDGE",EDGE,{"disambiguationData":[OSD([sQuery(id+"F5.wireOp",EDGE,"E5.top")])],"isStart":false});
            var Q2;
            Q2=makeQuery(id+"F4.opExtrude","CAP_EDGE",EDGE,{"disambiguationData":[OSD([sQuery(id+"F2.wireOp",EDGE,"E4.right")])],"isStart":false});
            fillet(context, id + "F7", {"entities" : qUnion([Q0, Q1, Q2]), "radius" : 1.5 * mm, "tangentPropagation" : true, "allowEdgeOverflow" : false});
        }
        {
            var Q0;
            {var subQ19=sQuery(id+"F2.wireOp",EDGE,"E4.top");var subQ20=sQuery(id+"F2.wireOp",EDGE,"E4.bottom");var subQ63=sQuery(id+"F0.wireOp",EDGE,"E0.sketch_text.stroke-2");var subQ66=sQuery(id+"F2.wireOp",EDGE,"E4.left");Q0=makeQuery(id+"F6.boolean.opBoolean","MERGE",FACE,{"derivedFrom":[makeQuery(id+"FaVoHrOpcFZXiYX_6.opBoolean","SPLIT",FACE,{"disambiguationData":[TD([makeQuery(id+"F1.opExtrude","SWEPT_FACE",FACE,{"disambiguationData":[OSD([subQ63])]})])],"derivedFrom":makeQuery(id+"F3.opExtrude","CAP_FACE",FACE,{"disambiguationData":[OSD([subQ20,subQ19,subQ66,sQuery(id+"F2.wireOp",EDGE,"E4.right")])],"isStart":false})}),makeQuery(id+"F6.opExtrude","SWEPT_FACE",FACE,{"disambiguationData":[OSD([sQuery(id+"F5.wireOp",EDGE,"E5.top")])]})]});}
            var sketch = newSketch(context, id + "F8", { "sketchPlane" : qUnion([Q0])});
            skCircle(sketch, "E6", {"center": v(-22.5, 0) * mm, "radius": 2 * mm});
            skSolve(sketch);
        }
        {
            var Q0;
            Q0=makeQuery(id+"F8.imprint","IMPRINT",FACE,{"disambiguationData":[TD([[makeQuery(id+"F8.imprint","IMPRINT",EDGE,{"derivedFrom":sQuery(id+"F8.wireOp",EDGE,"E6")}),1.0]])]});
            extrude(context, id + "F9", {"entities" : qUnion([Q0]), "operationType" : NewBodyOperationType.REMOVE, "oppositeDirection" : true, "depth" : 4 * mm});
        }
        {
            var Q0;
            Q0=makeQuery(id+"F3.opExtrude","CAP_EDGE",EDGE,{"disambiguationData":[OSD([sQuery(id+"F2.wireOp",EDGE,"E4.right")])],"isStart":false});
            fillet(context, id + "F10", {"entities" : qUnion([Q0]), "radius" : 1.5 * mm, "tangentPropagation" : true, "allowEdgeOverflow" : false});
        }
    });
